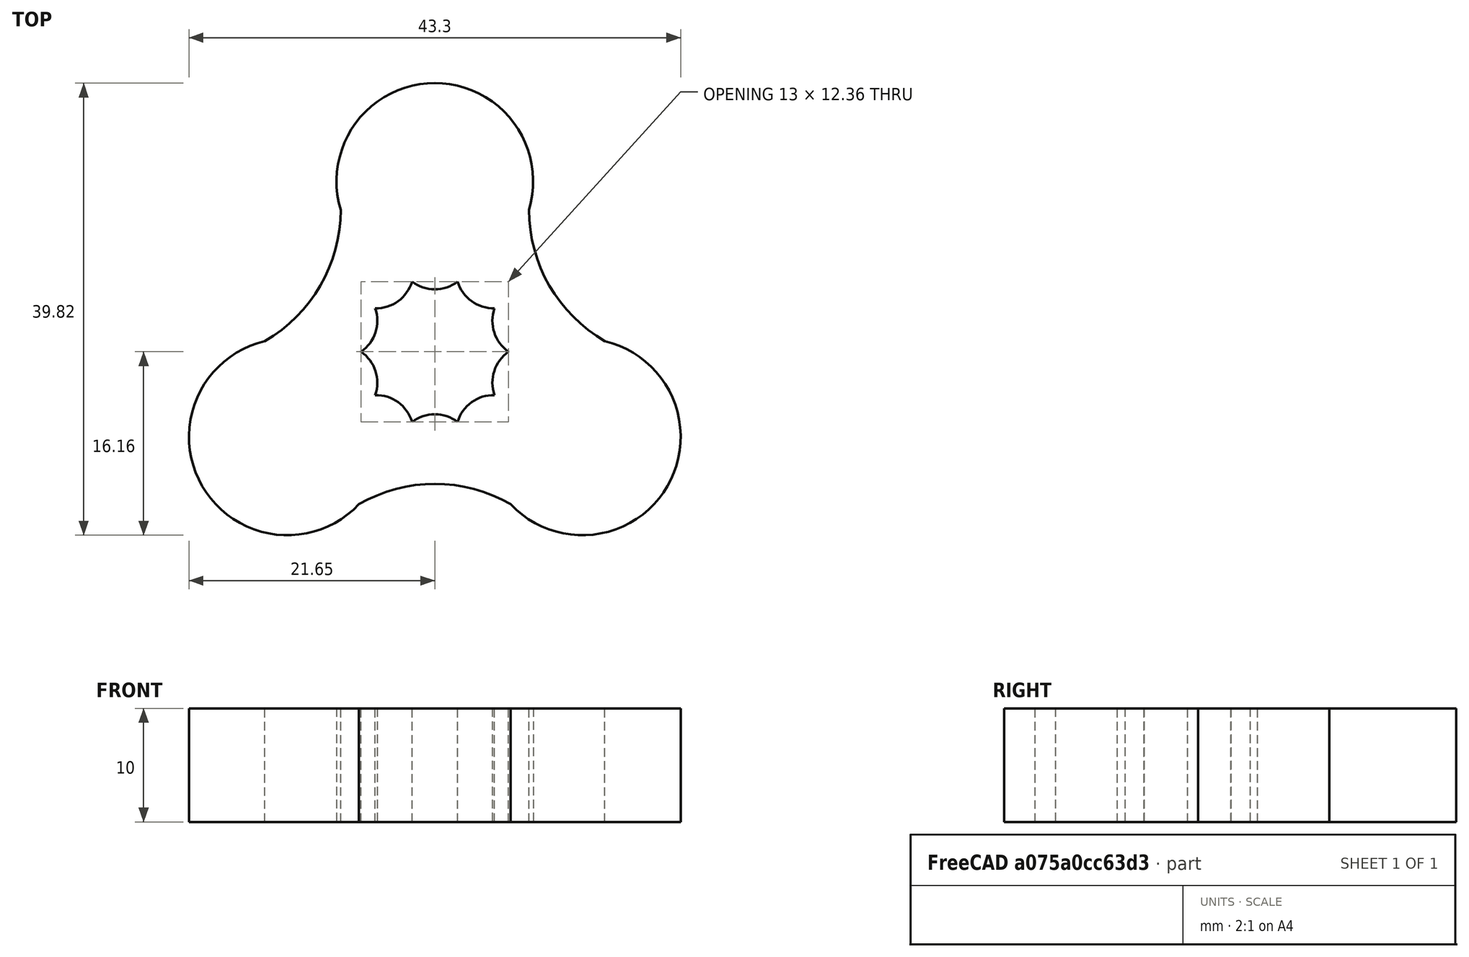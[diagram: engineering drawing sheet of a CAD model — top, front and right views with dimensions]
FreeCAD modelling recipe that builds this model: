
FCSTD DOCUMENT  (FreeCAD 0.19RUnknown)
Label: paint_tube_opener
License: All rights reserved
LicenseURL: http://en.wikipedia.org/wiki/All_rights_reserved
objects: Sketcher::SketchObject×1, PartDesign::Pad×1, PartDesign::Body×1, App::Part×1
note: 4 computed .brp shape members not serialized (recipe doc carries the construction recipe); baked Part::Feature solids carry a one-line shape summary decoded from their .brp

FEATURE [Sketcher::SketchObject] Sketch
  FullyConstrained = false
  MapMode = 5
  Support = -> [XY_Plane001]
  sketch-geometry (38):
    g0: Circle CenterX=0 CenterY=0 CenterZ=0 NormalX=0 NormalY=0 NormalZ=1 AngleXU=0 Radius=6.5
    g1: ArcOfCircle CenterX=-8.36869 CenterY=2.71915 CenterZ=0 NormalX=0 NormalY=0 NormalZ=1 AngleXU=0 Radius=3.29937 StartAngle=5.3145 EndAngle=6.62356
    g2: ArcOfCircle CenterX=-5.17214 CenterY=7.11884 CenterZ=0 NormalX=0 NormalY=0 NormalZ=1 AngleXU=0 Radius=3.29937 StartAngle=4.68618 EndAngle=5.99524
    g3: ArcOfCircle CenterX=0 CenterY=8.79937 CenterZ=0 NormalX=0 NormalY=0 NormalZ=1 AngleXU=0 Radius=3.29937 StartAngle=4.05786 EndAngle=5.36692
    g4: ArcOfCircle CenterX=5.17214 CenterY=7.11884 CenterZ=0 NormalX=0 NormalY=0 NormalZ=1 AngleXU=0 Radius=3.29937 StartAngle=3.42954 EndAngle=4.7386
    g5: ArcOfCircle CenterX=8.36869 CenterY=2.71915 CenterZ=0 NormalX=0 NormalY=0 NormalZ=1 AngleXU=0 Radius=3.29937 StartAngle=2.80122 EndAngle=4.11028
    g6: ArcOfCircle CenterX=8.36869 CenterY=-2.71915 CenterZ=0 NormalX=0 NormalY=0 NormalZ=1 AngleXU=0 Radius=3.29937 StartAngle=2.1729 EndAngle=3.48196
    g7: ArcOfCircle CenterX=5.17214 CenterY=-7.11884 CenterZ=0 NormalX=0 NormalY=0 NormalZ=1 AngleXU=0 Radius=3.29937 StartAngle=1.54458 EndAngle=2.85365
    g8: ArcOfCircle CenterX=9e-16 CenterY=-8.79937 CenterZ=0 NormalX=0 NormalY=0 NormalZ=1 AngleXU=0 Radius=3.29937 StartAngle=0.916266 EndAngle=2.22533
    g9: ArcOfCircle CenterX=-5.17214 CenterY=-7.11884 CenterZ=0 NormalX=0 NormalY=0 NormalZ=1 AngleXU=0 Radius=3.29937 StartAngle=0.287947 EndAngle=1.59701
    g10: ArcOfCircle CenterX=-8.36869 CenterY=-2.71915 CenterZ=0 NormalX=0 NormalY=0 NormalZ=1 AngleXU=0 Radius=3.29937 StartAngle=5.94281 EndAngle=7.25188
    g11: GeomPoint X=0 Y=5.5 Z=0
    g12: GeomPoint X=0 Y=-5.5 Z=0
    g13: LineSegment StartX=-5.25861 StartY=3.8206 StartZ=0 EndX=-2.00861 EndY=6.18187 EndZ=0
    g14: LineSegment StartX=-2.00861 StartY=6.18187 StartZ=0 EndX=2.00861 EndY=6.18187 EndZ=0
    g15: LineSegment StartX=2.00861 StartY=6.18187 StartZ=0 EndX=5.25861 EndY=3.8206 EndZ=0
    g16: LineSegment StartX=5.25861 StartY=3.8206 StartZ=0 EndX=6.5 EndY=0 EndZ=0
    g17: LineSegment StartX=6.5 StartY=0 StartZ=0 EndX=5.25861 EndY=-3.8206 EndZ=0
    g18: LineSegment StartX=5.25861 StartY=-3.8206 StartZ=0 EndX=2.00861 EndY=-6.18187 EndZ=0
    g19: LineSegment StartX=2.00861 StartY=-6.18187 StartZ=0 EndX=-2.00861 EndY=-6.18187 EndZ=0
    g20: LineSegment StartX=-2.00861 StartY=-6.18187 StartZ=0 EndX=-5.25861 EndY=-3.8206 EndZ=0
    g21: LineSegment StartX=-5.25861 StartY=-3.8206 StartZ=0 EndX=-6.5 EndY=0 EndZ=0
    g22: LineSegment StartX=-6.5 StartY=0 StartZ=0 EndX=-5.25861 EndY=3.8206 EndZ=0
    g23: Circle CenterX=0 CenterY=0 CenterZ=0 NormalX=0 NormalY=0 NormalZ=1 AngleXU=0 Radius=8.79937
    g24: Circle CenterX=0 CenterY=0 CenterZ=0 NormalX=0 NormalY=0 NormalZ=1 AngleXU=0 Radius=15
    g25: Circle CenterX=0 CenterY=0 CenterZ=0 NormalX=0 NormalY=0 NormalZ=1 AngleXU=0 Radius=25
    g26: LineSegment StartX=0 StartY=15 StartZ=0 EndX=-12.9904 EndY=-7.5 EndZ=0
    g27: LineSegment StartX=12.9904 StartY=-7.5 StartZ=0 EndX=-12.9904 EndY=-7.5 EndZ=0
    g28: LineSegment StartX=0 StartY=15 StartZ=0 EndX=12.9904 EndY=-7.5 EndZ=0
    g29: ArcOfCircle CenterX=21.6506 CenterY=12.5 CenterZ=0 NormalX=0 NormalY=0 NormalZ=1 AngleXU=0 Radius=13.3591 StartAngle=3.14159 EndAngle=4.18879
    g30: ArcOfCircle CenterX=0 CenterY=-25 CenterZ=0 NormalX=0 NormalY=0 NormalZ=1 AngleXU=0 Radius=13.3591 StartAngle=1.0472 EndAngle=2.0944
    g31: ArcOfCircle CenterX=-21.6506 CenterY=12.5 CenterZ=0 NormalX=0 NormalY=0 NormalZ=1 AngleXU=0 Radius=13.3591 StartAngle=5.23599 EndAngle=6.28319
    g32: LineSegment StartX=-21.6506 StartY=12.5 StartZ=0 EndX=21.6506 EndY=12.5 EndZ=0
    g33: LineSegment StartX=0 StartY=-25 StartZ=0 EndX=21.6506 EndY=12.5 EndZ=0
    g34: LineSegment StartX=0 StartY=-25 StartZ=0 EndX=-21.6506 EndY=12.5 EndZ=0
    g35: ArcOfCircle CenterX=-12.9904 CenterY=-7.5 CenterZ=0 NormalX=0 NormalY=0 NormalZ=1 AngleXU=0 Radius=8.66025 StartAngle=1.80155 EndAngle=5.52883
    g36: ArcOfCircle CenterX=12.9904 CenterY=-7.5 CenterZ=0 NormalX=0 NormalY=0 NormalZ=1 AngleXU=0 Radius=8.66025 StartAngle=3.89595 EndAngle=7.62323
    g37: ArcOfCircle CenterX=0 CenterY=15 CenterZ=0 NormalX=0 NormalY=0 NormalZ=1 AngleXU=0 Radius=8.66025 StartAngle=5.99034 EndAngle=9.71762
  constraints (108):
    c: Coincident(g0,g-1)
    c: PointOnObject(g1,g0)
    c: PointOnObject(g1,g0)
    c: Coincident(g2,g1)
    c: PointOnObject(g2,g0)
    c: Coincident(g3,g2)
    c: PointOnObject(g3,g0)
    c: Coincident(g4,g3)
    c: PointOnObject(g4,g0)
    c: Coincident(g5,g4)
    c: PointOnObject(g5,g0)
    c: Coincident(g6,g5)
    c: PointOnObject(g6,g0)
    c: Coincident(g7,g6)
    c: PointOnObject(g7,g0)
    c: Coincident(g8,g7)
    c: PointOnObject(g8,g0)
    c: Coincident(g9,g8)
    c: PointOnObject(g9,g0)
    c: Coincident(g10,g9)
    c: Coincident(g10,g1)
    c: PointOnObject(g11,g3)
    c: PointOnObject(g12,g8)
    c: PointOnObject(g12,g-2)
    c: PointOnObject(g11,g-2)
    c: DistanceY(g12,g11) = 11
    c: PointOnObject(g3,g-2)
    c: Diameter(g0) = 13
    c: Coincident(g13,g1)
    c: Coincident(g13,g2)
    c: Coincident(g14,g2)
    c: Coincident(g14,g3)
    c: Coincident(g15,g3)
    c: Coincident(g15,g4)
    c: Coincident(g16,g4)
    c: Coincident(g16,g5)
    c: Coincident(g17,g5)
    c: Coincident(g17,g6)
    c: Coincident(g18,g6)
    c: Coincident(g18,g7)
    c: Coincident(g19,g7)
    c: Coincident(g19,g8)
    c: Coincident(g20,g8)
    c: Coincident(g20,g9)
    c: Coincident(g21,g9)
    c: Coincident(g21,g1)
    c: Coincident(g22,g1)
    c: Coincident(g22,g1)
    c: Equal(g13,g14)
    c: Equal(g14,g15)
    c: Equal(g15,g16)
    c: Equal(g16,g17)
    c: Equal(g17,g18)
    c: Equal(g18,g19)
    c: Equal(g19,g20)
    c: Equal(g20,g21)
    c: Equal(g21,g22)
    c: Coincident(g23,g-1)
    c: PointOnObject(g2,g23)
    c: PointOnObject(g1,g23)
    c: PointOnObject(g5,g23)
    c: PointOnObject(g4,g23)
    c: PointOnObject(g6,g23)
    c: PointOnObject(g3,g23)
    c: PointOnObject(g7,g23)
    c: PointOnObject(g8,g23)
    c: PointOnObject(g9,g23)
    c: PointOnObject(g10,g23)
    c: Coincident(g24,g-1)
    c: Coincident(g25,g-1)
    c: PointOnObject(g26,g24)
    c: PointOnObject(g26,g24)
    c: PointOnObject(g27,g24)
    c: Coincident(g27,g26)
    c: Coincident(g28,g26)
    c: Coincident(g28,g27)
    c: Equal(g28,g27)
    c: Equal(g27,g26)
    c: PointOnObject(g26,g-2)
    c: Diameter(g24) = 30
    c: Diameter(g25) = 50
    c: PointOnObject(g29,g25)
    c: PointOnObject(g29,g24)
    c: PointOnObject(g29,g24)
    c: PointOnObject(g30,g25)
    c: PointOnObject(g30,g24)
    c: PointOnObject(g30,g24)
    c: PointOnObject(g31,g25)
    c: PointOnObject(g31,g24)
    c: PointOnObject(g31,g24)
    c: PointOnObject(g30,g-2)
    c: Coincident(g32,g31)
    c: Coincident(g32,g29)
    c: Horizontal(g32)
    c: Coincident(g33,g30)
    c: Coincident(g33,g29)
    c: Coincident(g34,g30)
    c: Coincident(g34,g31)
    c: Equal(g34,g32)
    c: Coincident(g35,g26)
    c: Coincident(g35,g30)
    c: Coincident(g35,g31)
    c: Coincident(g36,g27)
    c: Coincident(g36,g30)
    c: Coincident(g36,g29)
    c: Coincident(g37,g26)
    c: Coincident(g37,g31)
    c: Coincident(g37,g29)
FEATURE [PartDesign::Pad] Pad
  Direction = (1,1,1)
  Length = 10
  Length2 = 100
  Profile = -> Sketch
  Type = 0
FEATURE [PartDesign::Body] Body
  Group = -> [Sketch,Pad]
  Origin = -> Origin001
  Tip = -> Pad
FEATURE [App::Part] Part  label="Van Gogh"
  Group = -> [Body]
  Origin = -> Origin
